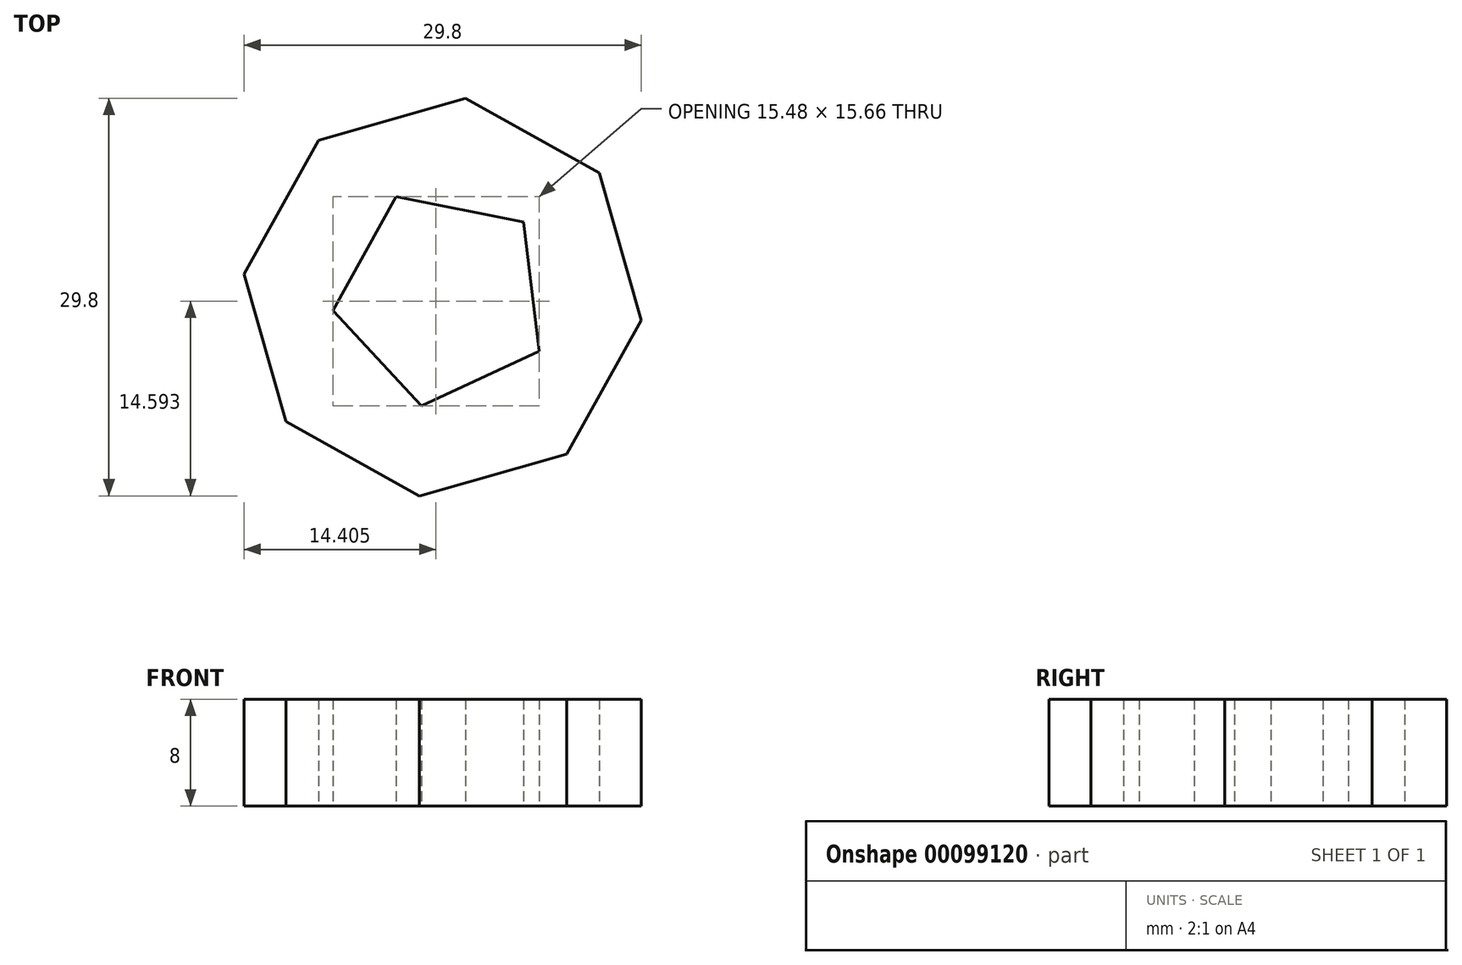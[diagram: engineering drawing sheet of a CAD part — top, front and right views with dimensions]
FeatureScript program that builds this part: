
annotation { "Feature Type Name" : "Feature", "Feature Type Description" : "" }
export const myFeature = defineFeature(function(context is Context, id is Id, definition is map)
    precondition{}
    {
        {
            var Q0;
            Q0=qCreatedBy(makeId("Top.planeOp"),FACE);
            var sketch = newSketch(context, id + "F0", { "sketchPlane" : qUnion([Q0])});
            skCircle(sketch, "E0.cCircle", {"center": v(0, 0) * mm, "radius": 13.86 * mm, "construction": true});
            skLineSegment(sketch, "E0.0", {"start": v(-14.9, 1.73) * mm, "end": v(-9.31, 11.76) * mm});
            skLineSegment(sketch, "E0.1", {"start": v(-9.31, 11.76) * mm, "end": v(1.73, 14.9) * mm});
            skLineSegment(sketch, "E0.2", {"start": v(1.73, 14.9) * mm, "end": v(11.76, 9.31) * mm});
            skLineSegment(sketch, "E0.3", {"start": v(11.76, 9.31) * mm, "end": v(14.9, -1.73) * mm});
            skLineSegment(sketch, "E0.4", {"start": v(14.9, -1.73) * mm, "end": v(9.31, -11.76) * mm});
            skLineSegment(sketch, "E0.5", {"start": v(9.31, -11.76) * mm, "end": v(-1.73, -14.9) * mm});
            skLineSegment(sketch, "E0.6", {"start": v(-1.73, -14.9) * mm, "end": v(-11.76, -9.31) * mm});
            skLineSegment(sketch, "E0.7", {"start": v(-11.76, -9.31) * mm, "end": v(-14.9, 1.73) * mm});
            skPoint(sketch, "E0.0.midPoint", {"position": v(-12.1, 6.75) * mm});
            skCircle(sketch, "E1.cCircle", {"center": v(0, 0) * mm, "radius": 6.7 * mm, "construction": true});
            skLineSegment(sketch, "E1.0", {"start": v(-8.23, -1) * mm, "end": v(-3.49, 7.52) * mm});
            skLineSegment(sketch, "E1.1", {"start": v(-3.49, 7.52) * mm, "end": v(6.08, 5.64) * mm});
            skLineSegment(sketch, "E1.2", {"start": v(6.08, 5.64) * mm, "end": v(7.24, -4.04) * mm});
            skLineSegment(sketch, "E1.3", {"start": v(7.24, -4.04) * mm, "end": v(-1.6, -8.14) * mm});
            skLineSegment(sketch, "E1.4", {"start": v(-1.6, -8.14) * mm, "end": v(-8.23, -1) * mm});
            skPoint(sketch, "E1.0.midPoint", {"position": v(-5.86, 3.27) * mm});
            skSolve(sketch);
        }
        {
            var Q0;
            Q0=makeQuery(id+"F0.imprint","IMPRINT",FACE,{"disambiguationData":[TD([[makeQuery(id+"F0.imprint","IMPRINT",EDGE,{"derivedFrom":sQuery(id+"F0.wireOp",EDGE,"E0.0")}),-1.0]])]});
            extrude(context, id + "F1", {"entities" : qUnion([Q0]), "depth" : 8 * mm});
        }
    });
